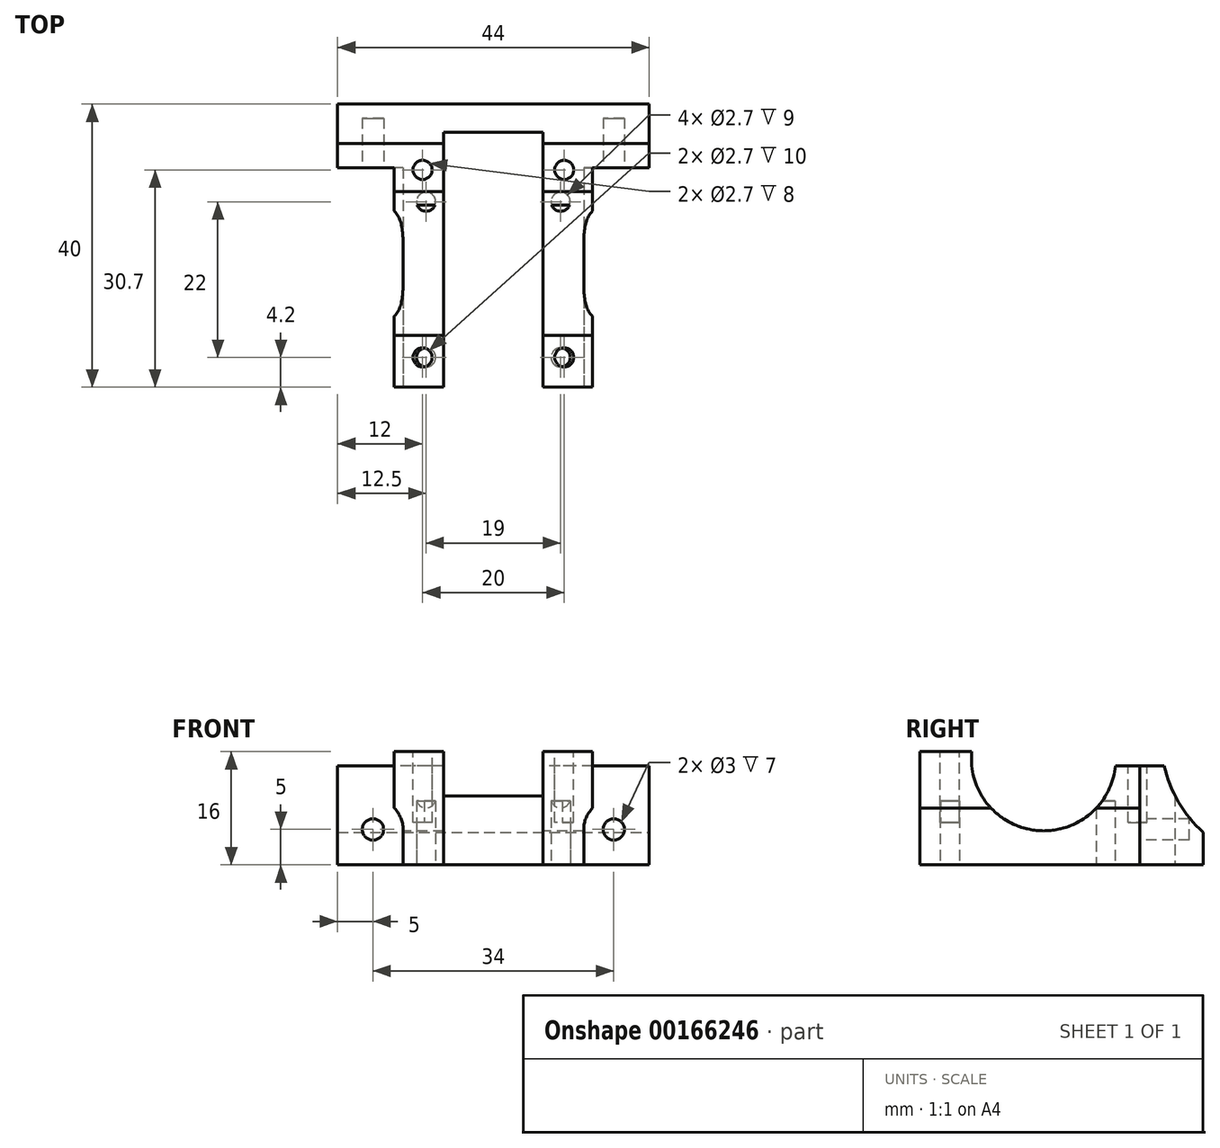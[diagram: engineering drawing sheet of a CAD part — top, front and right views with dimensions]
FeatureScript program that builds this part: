
annotation { "Feature Type Name" : "Feature", "Feature Type Description" : "" }
export const myFeature = defineFeature(function(context is Context, id is Id, definition is map)
    precondition{}
    {
        {
            var Q0;
            Q0=qCreatedBy(makeId("Top.planeOp"),FACE);
            var sketch = newSketch(context, id + "F0", { "sketchPlane" : qUnion([Q0])});
            skLineSegment(sketch, "E0.bottom", {"start": v(-14, 0) * mm, "end": v(-7, 0) * mm});
            skLineSegment(sketch, "E0.top", {"start": v(-14, 31) * mm, "end": v(-7, 31) * mm});
            skLineSegment(sketch, "E0.left", {"start": v(-14, 0) * mm, "end": v(-14, 31) * mm});
            skLineSegment(sketch, "E0.right", {"start": v(14, 0) * mm, "end": v(14, 31) * mm});
            skLineSegment(sketch, "E1", {"start": v(-14, 31) * mm, "end": v(-22, 31) * mm});
            skLineSegment(sketch, "E2", {"start": v(14, 31) * mm, "end": v(22, 31) * mm});
            skLineSegment(sketch, "E3", {"start": v(22, 40) * mm, "end": v(-22, 40) * mm});
            skLineSegment(sketch, "E4", {"start": v(-22, 40) * mm, "end": v(-22, 31) * mm});
            skLineSegment(sketch, "E5", {"start": v(22, 40) * mm, "end": v(22, 31) * mm});
            skLineSegment(sketch, "E6.left", {"start": v(-7, 31) * mm, "end": v(-7, 0) * mm});
            skLineSegment(sketch, "E6.right", {"start": v(7, 31) * mm, "end": v(7, 0) * mm});
            skLineSegment(sketch, "E7.trimOffspring", {"start": v(7, 0) * mm, "end": v(14, 0) * mm});
            skLineSegment(sketch, "E8", {"start": v(-7, 31) * mm, "end": v(-7, 36) * mm});
            skLineSegment(sketch, "E9", {"start": v(-7, 36) * mm, "end": v(7, 36) * mm});
            skLineSegment(sketch, "E10", {"start": v(7, 31) * mm, "end": v(7, 36) * mm});
            skLineSegment(sketch, "E11.trimOffspring", {"start": v(7, 31) * mm, "end": v(14, 31) * mm});
            skSolve(sketch);
        }
        {
            var Q0;
            Q0 = qSketchRegion(id + "F0", true);
            extrude(context, id + "F1", {"entities" : qUnion([Q0]), "depth" : 14 * mm});
        }
        {
            var Q0;
            Q0=makeQuery(id+"F1.opExtrude","CAP_FACE",FACE,{"disambiguationData":[OSD([sQuery(id+"F0.wireOp",EDGE,"E0.bottom"),sQuery(id+"F0.wireOp",EDGE,"E0.top"),sQuery(id+"F0.wireOp",EDGE,"E0.left"),sQuery(id+"F0.wireOp",EDGE,"E0.right"),sQuery(id+"F0.wireOp",EDGE,"E1"),sQuery(id+"F0.wireOp",EDGE,"E2"),sQuery(id+"F0.wireOp",EDGE,"E3"),sQuery(id+"F0.wireOp",EDGE,"E4"),sQuery(id+"F0.wireOp",EDGE,"E5"),sQuery(id+"F0.wireOp",EDGE,"E6.left"),sQuery(id+"F0.wireOp",EDGE,"E6.right"),sQuery(id+"F0.wireOp",EDGE,"E7.trimOffspring")])],"isStart":false});
            var sketch = newSketch(context, id + "F2", { "sketchPlane" : qUnion([Q0])});
            skCircle(sketch, "E12", {"center": v(-10, 4.2) * mm, "radius": 1.35 * mm});
            skCircle(sketch, "E13", {"center": v(-10, 30.7) * mm, "radius": 1.35 * mm});
            skCircle(sketch, "E14", {"center": v(10, 30.7) * mm, "radius": 1.35 * mm});
            skCircle(sketch, "E15", {"center": v(10, 4.2) * mm, "radius": 1.35 * mm});
            skSolve(sketch);
        }
        {
            var Q0;
            Q0 = qSketchRegion(id + "F2", true);
            extrude(context, id + "F3", {"entities" : qUnion([Q0]), "operationType" : NewBodyOperationType.REMOVE, "oppositeDirection" : true, "depth" : 8 * mm});
        }
        {
            var Q0;
            Q0=makeQuery(id+"F1.opExtrude","SWEPT_FACE",FACE,{"disambiguationData":[OSD([sQuery(id+"F0.wireOp",EDGE,"E0.left")])]});
            var sketch = newSketch(context, id + "F4", { "sketchPlane" : qUnion([Q0])});
            skCircle(sketch, "E16", {"center": v(-17.45, 15) * mm, "radius": 10.2 * mm});
            skSolve(sketch);
        }
        {
            var Q0;
            Q0 = qSketchRegion(id + "F4", true);
            extrude(context, id + "F5", {"entities" : qUnion([Q0]), "operationType" : NewBodyOperationType.REMOVE, "oppositeDirection" : true, "depth" : 30 * mm});
        }
        {
            var Q0;
            Q0=makeQuery(id+"F1.opExtrude","CAP_FACE",FACE,{"disambiguationData":[OSD([sQuery(id+"F0.wireOp",EDGE,"E0.bottom"),sQuery(id+"F0.wireOp",EDGE,"E0.top"),sQuery(id+"F0.wireOp",EDGE,"E0.left"),sQuery(id+"F0.wireOp",EDGE,"E0.right"),sQuery(id+"F0.wireOp",EDGE,"E1"),sQuery(id+"F0.wireOp",EDGE,"E2"),sQuery(id+"F0.wireOp",EDGE,"E3"),sQuery(id+"F0.wireOp",EDGE,"E4"),sQuery(id+"F0.wireOp",EDGE,"E5"),sQuery(id+"F0.wireOp",EDGE,"E6.left"),sQuery(id+"F0.wireOp",EDGE,"E6.right"),sQuery(id+"F0.wireOp",EDGE,"E7.trimOffspring")])],"isStart":true});
            var sketch = newSketch(context, id + "F6", { "sketchPlane" : qUnion([Q0])});
            skCircle(sketch, "E17", {"center": v(9.5, -4.2) * mm, "radius": 1.35 * mm});
            skCircle(sketch, "E18", {"center": v(-9.5, -4.2) * mm, "radius": 1.35 * mm});
            skCircle(sketch, "E19", {"center": v(9.5, -26.2) * mm, "radius": 1.35 * mm});
            skCircle(sketch, "E20", {"center": v(-9.5, -26.2) * mm, "radius": 1.35 * mm});
            skSolve(sketch);
        }
        {
            var Q0;
            Q0 = qSketchRegion(id + "F6", true);
            extrude(context, id + "F7", {"entities" : qUnion([Q0]), "operationType" : NewBodyOperationType.REMOVE, "oppositeDirection" : true, "depth" : 9 * mm});
        }
        {
            var Q0;
            Q0=makeQuery(id+"F1.opExtrude","SWEPT_FACE",FACE,{"disambiguationData":[OSD([sQuery(id+"F0.wireOp",EDGE,"E2")])]});
            var sketch = newSketch(context, id + "F8", { "sketchPlane" : qUnion([Q0])});
            skCircle(sketch, "E21", {"center": v(-17, 5) * mm, "radius": 1.5 * mm});
            skCircle(sketch, "E22", {"center": v(17, 5) * mm, "radius": 1.5 * mm});
            skSolve(sketch);
        }
        {
            var Q0;
            Q0 = qSketchRegion(id + "F8", true);
            extrude(context, id + "F9", {"entities" : qUnion([Q0]), "operationType" : NewBodyOperationType.REMOVE, "oppositeDirection" : true, "depth" : 7 * mm});
        }
        {
            var Q0;
            Q0=makeQuery(id+"F1.opExtrude","SWEPT_FACE",FACE,{"disambiguationData":[OSD([sQuery(id+"F0.wireOp",EDGE,"E5")])]});
            var sketch = newSketch(context, id + "F10", { "sketchPlane" : qUnion([Q0])});
            skCircle(sketch, "E23", {"center": v(52, 18) * mm, "radius": 18 * mm});
            skSolve(sketch);
        }
        {
            var Q0;
            Q0 = qSketchRegion(id + "F10", true);
            extrude(context, id + "F11", {"entities" : qUnion([Q0]), "operationType" : NewBodyOperationType.REMOVE, "endBound" : BoundingType.THROUGH_ALL, "oppositeDirection" : true, "depth" : 25 * mm});
        }
        {
            var Q0;
            Q0=makeQuery(id+"F1.opExtrude","SWEPT_FACE",FACE,{"disambiguationData":[OSD([sQuery(id+"F0.wireOp",EDGE,"E7.trimOffspring")])]});
            var sketch = newSketch(context, id + "F12", { "sketchPlane" : qUnion([Q0])});
            skArc(sketch, "E24", {"start": v(-12.75, 5) * mm, "mid": v(-18.8, 8.85) * mm, "end": v(-19.71, 1.73) * mm});
            skArc(sketch, "E25", {"start": v(19.71, 1.73) * mm, "mid": v(18.8, 8.85) * mm, "end": v(12.75, 5) * mm});
            skLineSegment(sketch, "E26", {"start": v(-12.75, 5) * mm, "end": v(-12.75, -4.05) * mm});
            skLineSegment(sketch, "E27", {"start": v(12.75, 5) * mm, "end": v(12.75, -4.05) * mm});
            skLineSegment(sketch, "E28", {"start": v(-12.75, -4.05) * mm, "end": v(-19.71, 1.73) * mm});
            skLineSegment(sketch, "E29", {"start": v(12.75, -4.05) * mm, "end": v(19.71, 1.73) * mm});
            skSolve(sketch);
        }
        {
            var Q0;
            Q0 = qSketchRegion(id + "F12", true);
            var Q1;
            Q1=makeQuery(id+"F1.opExtrude","SWEPT_FACE",FACE,{"disambiguationData":[OSD([sQuery(id+"F0.wireOp",EDGE,"E1")])]});
            extrude(context, id + "F13", {"entities" : qUnion([Q0]), "operationType" : NewBodyOperationType.REMOVE, "endBound" : BoundingType.UP_TO_SURFACE, "oppositeDirection" : true, "endBoundEntityFace" : qUnion([Q1]), "depth" : 25 * mm});
        }
        {
            var Q0;
            {var subQ0=sQuery(id+"F0.wireOp",EDGE,"E7.trimOffspring");var subQ1=sQuery(id+"F0.wireOp",EDGE,"E10");var subQ2=sQuery(id+"F0.wireOp",EDGE,"E6.right");var subQ3=sQuery(id+"F0.wireOp",EDGE,"E0.right");Q0=makeQuery(id+"F5.boolean.opBoolean","SPLIT",FACE,{"disambiguationData":[TD([makeQuery(id+"F1.opExtrude","SWEPT_FACE",FACE,{"disambiguationData":[OSD([subQ0])]})])],"derivedFrom":makeQuery(id+"F1.opExtrude","CAP_FACE",FACE,{"disambiguationData":[OSD([sQuery(id+"F0.wireOp",EDGE,"E0.bottom"),sQuery(id+"F0.wireOp",EDGE,"E0.left"),subQ3,sQuery(id+"F0.wireOp",EDGE,"E1"),sQuery(id+"F0.wireOp",EDGE,"E2"),sQuery(id+"F0.wireOp",EDGE,"E3"),sQuery(id+"F0.wireOp",EDGE,"E4"),sQuery(id+"F0.wireOp",EDGE,"E5"),sQuery(id+"F0.wireOp",EDGE,"E6.left"),subQ2,subQ0,sQuery(id+"F0.wireOp",EDGE,"E8"),sQuery(id+"F0.wireOp",EDGE,"E9"),subQ1])],"isStart":false})});}
            var sketch = newSketch(context, id + "F14", { "sketchPlane" : qUnion([Q0])});
            skCircle(sketch, "E30.0", {"center": v(10, 4.2) * mm, "radius": 1.35 * mm});
            skLineSegment(sketch, "E31.0", {"start": v(14, 0) * mm, "end": v(14, 7.3) * mm});
            skLineSegment(sketch, "E32.0", {"start": v(7, 0) * mm, "end": v(14, 0) * mm});
            skLineSegment(sketch, "E33.0", {"start": v(7, 7.3) * mm, "end": v(7, 0) * mm});
            skLineSegment(sketch, "E34.0", {"start": v(7, 7.3) * mm, "end": v(14, 7.3) * mm});
            skLineSegment(sketch, "E35.0", {"start": v(-7, 7.3) * mm, "end": v(-7, 0) * mm});
            skLineSegment(sketch, "E36.0.0", {"start": v(-14, 7.3) * mm, "end": v(-7, 7.3) * mm});
            skLineSegment(sketch, "E36.0.1", {"start": v(-14, 7.3) * mm, "end": v(-14, 0) * mm});
            skLineSegment(sketch, "E36.0.2", {"start": v(-14, 0) * mm, "end": v(-7, 0) * mm});
            skLineSegment(sketch, "E36.0.3", {"start": v(-7, 0) * mm, "end": v(-7, 7.3) * mm});
            skCircle(sketch, "E37.0", {"center": v(-10, 4.2) * mm, "radius": 1.35 * mm});
            skSolve(sketch);
        }
        {
            var Q0;
            Q0 = qSketchRegion(id + "F14", true);
            extrude(context, id + "F15", {"entities" : qUnion([Q0]), "operationType" : NewBodyOperationType.ADD, "depth" : 2 * mm});
        }
    });
